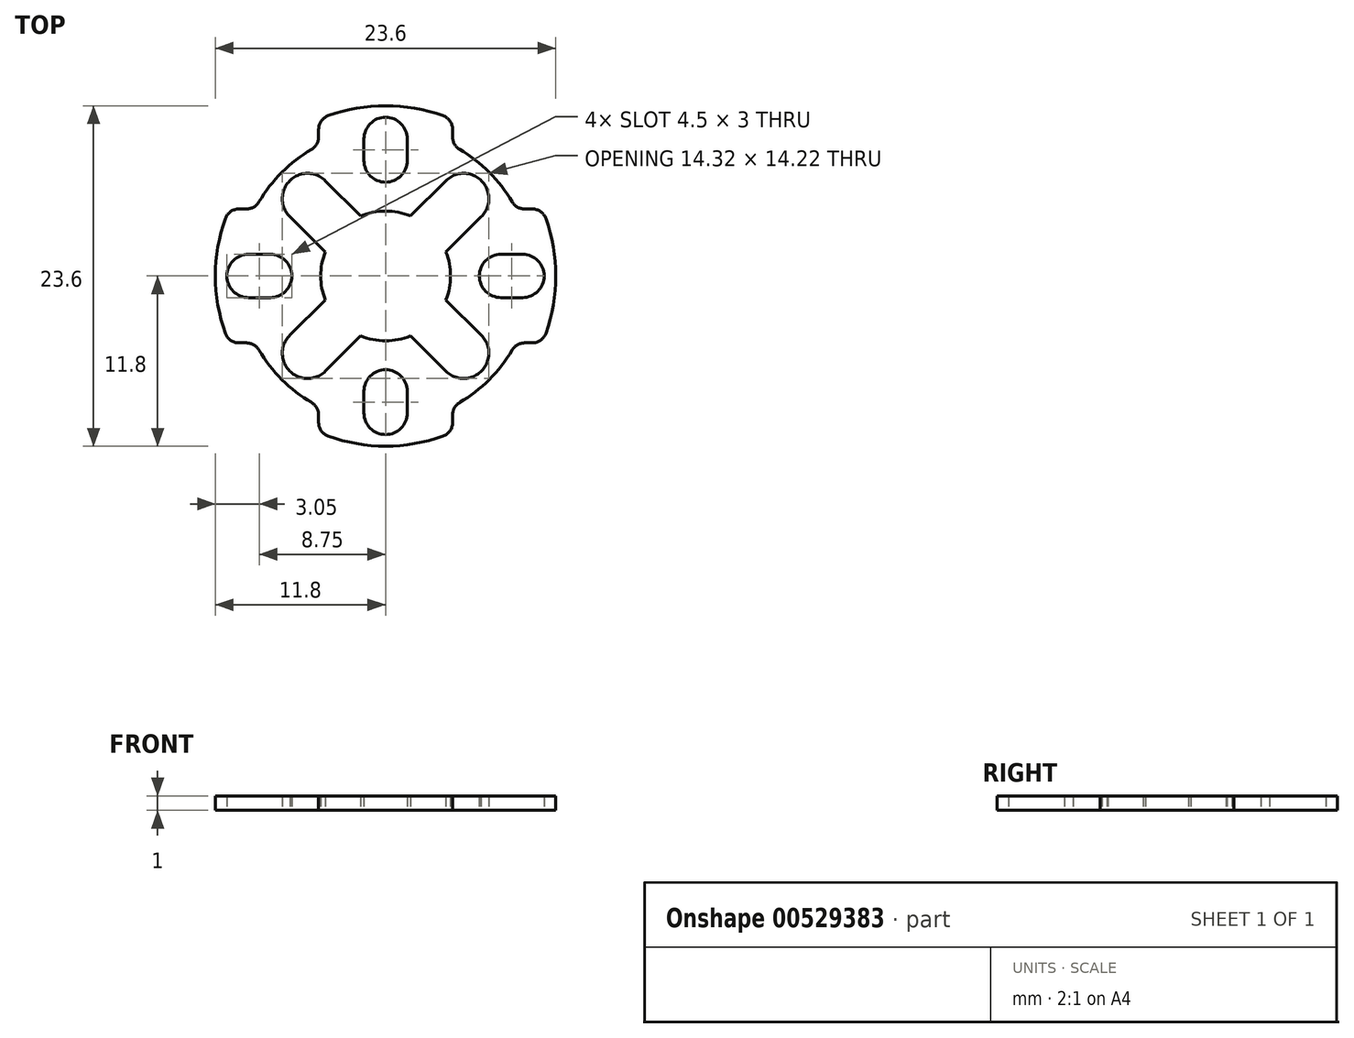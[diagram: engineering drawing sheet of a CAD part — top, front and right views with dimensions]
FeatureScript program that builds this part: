
annotation { "Feature Type Name" : "Feature", "Feature Type Description" : "" }
export const myFeature = defineFeature(function(context is Context, id is Id, definition is map)
    precondition{}
    {
        {
            var Q0;
            Q0=qCreatedBy(makeId("Top.planeOp"),FACE);
            var sketch = newSketch(context, id + "F0", { "sketchPlane" : qUnion([Q0])});
            skLineSegment(sketch, "E0", {"start": v(0, 0) * mm, "end": v(-33.45, 33.45) * mm, "construction": true});
            skArc(sketch, "E1", {"start": v(1.5, 9.5) * mm, "mid": v(0, 11) * mm, "end": v(-1.5, 9.5) * mm});
            skPoint(sketch, "E2.center.orphan", {"position": v(0, 8) * mm});
            skArc(sketch, "E3", {"start": v(-1.5, 8) * mm, "mid": v(0, 6.5) * mm, "end": v(1.5, 8) * mm});
            skLineSegment(sketch, "E4", {"start": v(1.5, 9.5) * mm, "end": v(1.5, 8) * mm});
            skLineSegment(sketch, "E5", {"start": v(-1.5, 9.5) * mm, "end": v(-1.5, 8) * mm});
            skArc(sketch, "E6", {"start": v(4.64, 10.85) * mm, "mid": v(0.36, 11.8) * mm, "end": v(-3.98, 11.1) * mm});
            skLineSegment(sketch, "E7", {"start": v(-1.73, 4.15) * mm, "end": v(-4.17, 6.6) * mm});
            skLineSegment(sketch, "E8", {"start": v(-4.18, 1.66) * mm, "end": v(-6.62, 4.1) * mm});
            skArc(sketch, "E9", {"start": v(-4.17, 6.6) * mm, "mid": v(-6.66, 6.58) * mm, "end": v(-6.62, 4.1) * mm});
            skArc(sketch, "E10", {"start": v(-5.14, 8.77) * mm, "mid": v(-6.21, 8.04) * mm, "end": v(-7.19, 7.19) * mm});
            skLineSegment(sketch, "E11", {"start": v(-4.64, 10.17) * mm, "end": v(-4.64, 9.63) * mm});
            skPoint(sketch, "E12.visualSharp", {"position": v(-4.64, 9.04) * mm});
            skArc(sketch, "E12.filletArc", {"start": v(-5.14, 8.77) * mm, "mid": v(-4.77, 9.14) * mm, "end": v(-4.64, 9.63) * mm});
            skPoint(sketch, "E13.visualSharp", {"position": v(-4.64, 10.85) * mm});
            skArc(sketch, "E13.filletArc", {"start": v(-3.98, 11.1) * mm, "mid": v(-4.46, 10.74) * mm, "end": v(-4.64, 10.17) * mm});
            skLineSegment(sketch, "E14.MirrorCS", {"start": v(4.64, 10.17) * mm, "end": v(4.64, 9.63) * mm});
            skArc(sketch, "E15.MirrorCS", {"start": v(5.14, 8.77) * mm, "mid": v(4.77, 9.14) * mm, "end": v(4.64, 9.63) * mm});
            skArc(sketch, "E16.MirrorCS", {"start": v(5.14, 8.77) * mm, "mid": v(6.21, 8.04) * mm, "end": v(7.19, 7.19) * mm});
            skPoint(sketch, "E17.MirrorP", {"position": v(4.64, 9.04) * mm});
            skPoint(sketch, "E18.MirrorP", {"position": v(4.64, 10.85) * mm});
            skArc(sketch, "E19.MirrorCS", {"start": v(3.98, 11.1) * mm, "mid": v(4.46, 10.74) * mm, "end": v(4.64, 10.17) * mm});
            skLineSegment(sketch, "E20.MirrorCS", {"start": v(1.73, 4.15) * mm, "end": v(4.17, 6.6) * mm});
            skArc(sketch, "E21.MirrorCS", {"start": v(4.17, 6.6) * mm, "mid": v(6.66, 6.58) * mm, "end": v(6.62, 4.1) * mm});
            skLineSegment(sketch, "E22.MirrorCS", {"start": v(4.18, 1.66) * mm, "end": v(6.62, 4.1) * mm});
            skLineSegment(sketch, "E23.MirrorCS", {"start": v(4.64, -10.17) * mm, "end": v(4.64, -9.63) * mm});
            skLineSegment(sketch, "E24.MirrorCS", {"start": v(-4.64, -10.17) * mm, "end": v(-4.64, -9.63) * mm});
            skArc(sketch, "E25.MirrorCS", {"start": v(-5.14, -8.77) * mm, "mid": v(-4.77, -9.14) * mm, "end": v(-4.64, -9.63) * mm});
            skPoint(sketch, "E26.MirrorP", {"position": v(4.64, -10.85) * mm});
            skArc(sketch, "E27.MirrorCS", {"start": v(-3.98, -11.1) * mm, "mid": v(-4.46, -10.74) * mm, "end": v(-4.64, -10.17) * mm});
            skArc(sketch, "E28.MirrorCS", {"start": v(3.98, -11.1) * mm, "mid": v(4.46, -10.74) * mm, "end": v(4.64, -10.17) * mm});
            skArc(sketch, "E29.MirrorCS", {"start": v(5.14, -8.77) * mm, "mid": v(4.77, -9.14) * mm, "end": v(4.64, -9.63) * mm});
            skArc(sketch, "E30.MirrorCS", {"start": v(-4.17, -6.6) * mm, "mid": v(-6.66, -6.58) * mm, "end": v(-6.62, -4.1) * mm});
            skArc(sketch, "E31.MirrorCS", {"start": v(-5.14, -8.77) * mm, "mid": v(-6.21, -8.04) * mm, "end": v(-7.19, -7.19) * mm});
            skPoint(sketch, "E32.MirrorP", {"position": v(-4.64, -9.04) * mm});
            skLineSegment(sketch, "E33.MirrorCS", {"start": v(1.5, -9.5) * mm, "end": v(1.5, -8) * mm});
            skLineSegment(sketch, "E34.MirrorCS", {"start": v(-1.5, -9.5) * mm, "end": v(-1.5, -8) * mm});
            skArc(sketch, "E35.MirrorCS", {"start": v(-1.5, -8) * mm, "mid": v(0, -6.5) * mm, "end": v(1.5, -8) * mm});
            skPoint(sketch, "E36.MirrorP", {"position": v(-4.64, -10.85) * mm});
            skArc(sketch, "E37.MirrorCS", {"start": v(5.14, -8.77) * mm, "mid": v(6.21, -8.04) * mm, "end": v(7.19, -7.19) * mm});
            skLineSegment(sketch, "E38.MirrorCS", {"start": v(-1.73, -4.15) * mm, "end": v(-4.17, -6.6) * mm});
            skPoint(sketch, "E39.MirrorP", {"position": v(4.64, -9.04) * mm});
            skArc(sketch, "E40.MirrorCS", {"start": v(1.5, -9.5) * mm, "mid": v(0, -11) * mm, "end": v(-1.5, -9.5) * mm});
            skArc(sketch, "E41.MirrorCS", {"start": v(4.17, -6.6) * mm, "mid": v(6.66, -6.58) * mm, "end": v(6.62, -4.1) * mm});
            skLineSegment(sketch, "E42.MirrorCS", {"start": v(1.73, -4.15) * mm, "end": v(4.17, -6.6) * mm});
            skLineSegment(sketch, "E43.MirrorCS", {"start": v(-4.18, -1.66) * mm, "end": v(-6.62, -4.1) * mm});
            skLineSegment(sketch, "E44.MirrorCS", {"start": v(4.18, -1.66) * mm, "end": v(6.62, -4.1) * mm});
            skArc(sketch, "E45.MirrorCS", {"start": v(4.64, -10.85) * mm, "mid": v(0.36, -11.8) * mm, "end": v(-3.98, -11.1) * mm});
            skLineSegment(sketch, "E46.MirrorCS", {"start": v(10.17, 4.64) * mm, "end": v(9.63, 4.64) * mm});
            skLineSegment(sketch, "E47.MirrorCS", {"start": v(10.17, -4.64) * mm, "end": v(9.63, -4.64) * mm});
            skArc(sketch, "E48.MirrorCS", {"start": v(8.77, 5.14) * mm, "mid": v(9.14, 4.77) * mm, "end": v(9.63, 4.64) * mm});
            skArc(sketch, "E49.MirrorCS", {"start": v(11.1, -3.98) * mm, "mid": v(10.74, -4.46) * mm, "end": v(10.17, -4.64) * mm});
            skArc(sketch, "E50.MirrorCS", {"start": v(11.1, 3.98) * mm, "mid": v(10.74, 4.46) * mm, "end": v(10.17, 4.64) * mm});
            skPoint(sketch, "E51.MirrorP", {"position": v(10.85, 4.64) * mm});
            skArc(sketch, "E52.MirrorCS", {"start": v(8.77, -5.14) * mm, "mid": v(9.14, -4.77) * mm, "end": v(9.63, -4.64) * mm});
            skArc(sketch, "E53.MirrorCS", {"start": v(8.77, -5.14) * mm, "mid": v(8.04, -6.21) * mm, "end": v(7.19, -7.19) * mm});
            skLineSegment(sketch, "E54.MirrorCS", {"start": v(9.5, 1.5) * mm, "end": v(8, 1.5) * mm});
            skPoint(sketch, "E55.MirrorP", {"position": v(9.04, -4.64) * mm});
            skArc(sketch, "E56.MirrorCS", {"start": v(11.1, 3.98) * mm, "mid": v(11.8, 0) * mm, "end": v(11.1, -3.98) * mm});
            skPoint(sketch, "E57.MirrorP", {"position": v(10.85, -4.64) * mm});
            skPoint(sketch, "E58.MirrorP", {"position": v(8, 0) * mm});
            skArc(sketch, "E59.MirrorCS", {"start": v(8.77, 5.14) * mm, "mid": v(8.04, 6.21) * mm, "end": v(7.19, 7.19) * mm});
            skPoint(sketch, "E60.MirrorP", {"position": v(9.04, 4.64) * mm});
            skLineSegment(sketch, "E61.MirrorCS", {"start": v(9.5, -1.5) * mm, "end": v(8, -1.5) * mm});
            skArc(sketch, "E62.MirrorCS", {"start": v(9.5, 1.5) * mm, "mid": v(11, 0) * mm, "end": v(9.5, -1.5) * mm});
            skArc(sketch, "E63.MirrorCS", {"start": v(8, -1.5) * mm, "mid": v(6.5, 0) * mm, "end": v(8, 1.5) * mm});
            skLineSegment(sketch, "E64.MirrorCS", {"start": v(-9.5, 1.5) * mm, "end": v(-8, 1.5) * mm});
            skLineSegment(sketch, "E65.MirrorCS", {"start": v(-9.5, -1.5) * mm, "end": v(-8, -1.5) * mm});
            skArc(sketch, "E66.MirrorCS", {"start": v(-8, -1.5) * mm, "mid": v(-6.5, 0) * mm, "end": v(-8, 1.5) * mm});
            skArc(sketch, "E67.MirrorCS", {"start": v(-9.5, 1.5) * mm, "mid": v(-11, 0) * mm, "end": v(-9.5, -1.5) * mm});
            skArc(sketch, "E68.MirrorCS", {"start": v(-8.77, 5.14) * mm, "mid": v(-8.04, 6.21) * mm, "end": v(-7.19, 7.19) * mm});
            skLineSegment(sketch, "E69.MirrorCS", {"start": v(0, 0) * mm, "end": v(33.45, -33.45) * mm, "construction": true});
            skLineSegment(sketch, "E70.MirrorCS", {"start": v(-10.17, -4.64) * mm, "end": v(-9.63, -4.64) * mm});
            skArc(sketch, "E71.MirrorCS", {"start": v(-8.77, -5.14) * mm, "mid": v(-9.14, -4.77) * mm, "end": v(-9.63, -4.64) * mm});
            skPoint(sketch, "E72.MirrorP", {"position": v(-9.04, -4.64) * mm});
            skPoint(sketch, "E73.MirrorP", {"position": v(-10.85, -4.64) * mm});
            skArc(sketch, "E74.MirrorCS", {"start": v(-8.77, -5.14) * mm, "mid": v(-8.04, -6.21) * mm, "end": v(-7.19, -7.19) * mm});
            skLineSegment(sketch, "E75.MirrorCS", {"start": v(-10.17, 4.64) * mm, "end": v(-9.63, 4.64) * mm});
            skArc(sketch, "E76.MirrorCS", {"start": v(-11.1, 3.98) * mm, "mid": v(-10.74, 4.46) * mm, "end": v(-10.17, 4.64) * mm});
            skArc(sketch, "E77.MirrorCS", {"start": v(-8.77, 5.14) * mm, "mid": v(-9.14, 4.77) * mm, "end": v(-9.63, 4.64) * mm});
            skPoint(sketch, "E78.MirrorP", {"position": v(-10.85, 4.64) * mm});
            skPoint(sketch, "E79.MirrorP", {"position": v(-9.04, 4.64) * mm});
            skArc(sketch, "E80.MirrorCS", {"start": v(-11.1, 3.98) * mm, "mid": v(-11.8, 0) * mm, "end": v(-11.1, -3.98) * mm});
            skArc(sketch, "E81.MirrorCS", {"start": v(-11.1, -3.98) * mm, "mid": v(-10.74, -4.46) * mm, "end": v(-10.17, -4.64) * mm});
            skPoint(sketch, "E82.end.orphan", {"position": v(-3.8, -1.27) * mm});
            skPoint(sketch, "E83.MirrorCS.start.orphan", {"position": v(1.34, -3.77) * mm});
            skPoint(sketch, "E84.orphan", {"position": v(-1.34, -3.77) * mm});
            skPoint(sketch, "E85.trimOffspring.end.orphan", {"position": v(3.8, 1.27) * mm});
            skPoint(sketch, "E85.trimOffspring.start.orphan", {"position": v(3.8, -1.27) * mm});
            skPoint(sketch, "E86.trimOffspring.start.orphan", {"position": v(1.34, 3.77) * mm});
            skPoint(sketch, "E87.orphan", {"position": v(-3.8, 1.27) * mm});
            skPoint(sketch, "E88.orphan", {"position": v(-1.34, 3.77) * mm});
            skArc(sketch, "E89", {"start": v(-4.18, 1.66) * mm, "mid": v(-4.5, 0) * mm, "end": v(-4.18, -1.66) * mm});
            skArc(sketch, "E90.trimOffspring", {"start": v(-1.73, -4.15) * mm, "mid": v(0, -4.5) * mm, "end": v(1.73, -4.15) * mm});
            skArc(sketch, "E91.trimOffspring", {"start": v(1.73, 4.15) * mm, "mid": v(0, 4.5) * mm, "end": v(-1.73, 4.15) * mm});
            skArc(sketch, "E92.trimOffspring", {"start": v(4.18, -1.66) * mm, "mid": v(4.5, 0) * mm, "end": v(4.18, 1.66) * mm});
            skCircle(sketch, "E93", {"center": v(0, 0) * mm, "radius": 13.85 * mm, "construction": true});
            skCircle(sketch, "E94", {"center": v(0, 0) * mm, "radius": 9.5 * mm, "construction": true});
            skCircle(sketch, "E95", {"center": v(0, 0) * mm, "radius": 8 * mm, "construction": true});
            skSolve(sketch);
        }
        {
            var Q0;
            Q0 = qSketchRegion(id + "F0", true);
            extrude(context, id + "F1", {"entities" : qUnion([Q0]), "depth" : 1 * mm, "offsetDistance" : 25 * mm});
        }
    });
